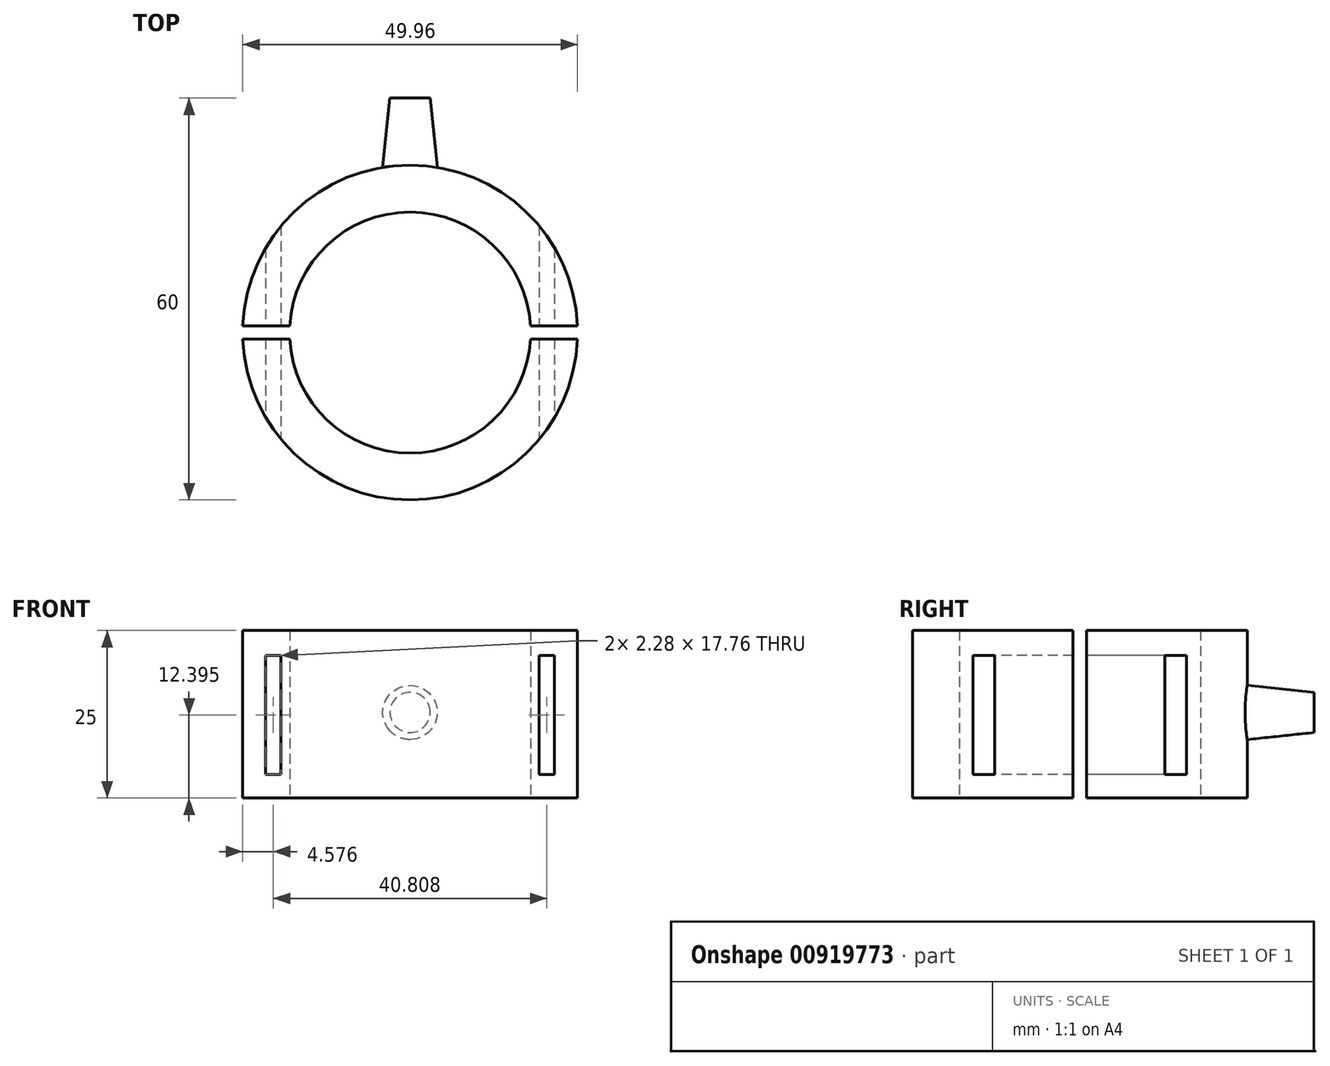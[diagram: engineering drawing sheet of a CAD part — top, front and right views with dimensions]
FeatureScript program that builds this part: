
annotation { "Feature Type Name" : "Feature", "Feature Type Description" : "" }
export const myFeature = defineFeature(function(context is Context, id is Id, definition is map)
    precondition{}
    {
        {
            var Q0;
            Q0=qCreatedBy(makeId("Top.planeOp"),FACE);
            var sketch = newSketch(context, id + "F0", { "sketchPlane" : qUnion([Q0])});
            skArc(sketch, "E0", {"start": v(-17.97, -1) * mm, "mid": v(0, -18) * mm, "end": v(17.97, -1) * mm});
            skArc(sketch, "E1.0", {"start": v(-24.98, -1) * mm, "mid": v(0, -25) * mm, "end": v(24.98, -1) * mm});
            skLineSegment(sketch, "E2.bottom", {"start": v(24.98, -1) * mm, "end": v(17.97, -1) * mm});
            skLineSegment(sketch, "E2.top", {"start": v(24.98, 1) * mm, "end": v(17.97, 1) * mm});
            skArc(sketch, "E3.trimOffspring", {"start": v(17.97, 1) * mm, "mid": v(0, 18) * mm, "end": v(-17.97, 1) * mm});
            skArc(sketch, "E4.trimOffspring", {"start": v(24.98, 1) * mm, "mid": v(0, 25) * mm, "end": v(-24.98, 1) * mm});
            skPoint(sketch, "E2.left.end.orphan", {"position": v(28.5, 1) * mm});
            skPoint(sketch, "E2.left.start.orphan", {"position": v(28.5, -1) * mm});
            skLineSegment(sketch, "E5.trimOffspring", {"start": v(-17.97, 1) * mm, "end": v(-24.98, 1) * mm});
            skLineSegment(sketch, "E6.trimOffspring", {"start": v(-17.97, -1) * mm, "end": v(-24.98, -1) * mm});
            skPoint(sketch, "E2.right.end.orphan", {"position": v(-28.5, 1) * mm});
            skPoint(sketch, "E7.orphan", {"position": v(-28.5, -1) * mm});
            skSolve(sketch);
        }
        {
            var Q0;
            Q0=makeQuery(id+"F0.imprint","IMPRINT",FACE,{"disambiguationData":[TD([[makeQuery(id+"F0.imprint","IMPRINT",EDGE,{"derivedFrom":sQuery(id+"F0.wireOp",EDGE,"E2.top")}),-1.0]])]});
            var Q1;
            Q1=makeQuery(id+"F0.imprint","IMPRINT",FACE,{"disambiguationData":[TD([[makeQuery(id+"F0.imprint","IMPRINT",EDGE,{"derivedFrom":sQuery(id+"F0.wireOp",EDGE,"E0")}),-1.0]])]});
            extrude(context, id + "F1", {"entities" : qUnion([Q0, Q1]), "depth" : 25 * mm, "offsetDistance" : 25 * mm});
        }
        {
            var Q0;
            Q0=qCreatedBy(makeId("Front.planeOp"),FACE);
            var sketch = newSketch(context, id + "F2", { "sketchPlane" : qUnion([Q0])});
            skLineSegment(sketch, "E8.bottom", {"start": v(21.54, 21.28) * mm, "end": v(19.26, 21.28) * mm});
            skLineSegment(sketch, "E8.top", {"start": v(21.54, 3.51) * mm, "end": v(19.26, 3.51) * mm});
            skLineSegment(sketch, "E8.left", {"start": v(21.54, 21.28) * mm, "end": v(21.54, 3.51) * mm});
            skLineSegment(sketch, "E8.right", {"start": v(19.26, 21.28) * mm, "end": v(19.26, 3.51) * mm});
            skPoint(sketch, "E8.middle", {"position": v(20.4, 12.4) * mm});
            skPoint(sketch, "E9.MirrorP", {"position": v(-20.4, 12.4) * mm});
            skLineSegment(sketch, "E10.MirrorCS", {"start": v(-21.54, 21.28) * mm, "end": v(-21.54, 3.51) * mm});
            skLineSegment(sketch, "E11.MirrorCS", {"start": v(-21.54, 21.28) * mm, "end": v(-19.26, 21.28) * mm});
            skLineSegment(sketch, "E12.MirrorCS", {"start": v(-19.26, 21.28) * mm, "end": v(-19.26, 3.51) * mm});
            skLineSegment(sketch, "E13.MirrorCS", {"start": v(-21.54, 3.51) * mm, "end": v(-19.26, 3.51) * mm});
            skSolve(sketch);
        }
        {
            var Q0;
            Q0 = qSketchRegion(id + "F2", true);
            extrude(context, id + "F3", {"entities" : qUnion([Q0]), "operationType" : NewBodyOperationType.REMOVE, "oppositeDirection" : true, "depth" : 25 * mm, "offsetDistance" : 25 * mm, "hasSecondDirection" : true, "secondDirectionOppositeDirection" : false, "secondDirectionDepth" : 25 * mm});
        }
        {
            var Q0;
            Q0=qCreatedBy(makeId("Front.planeOp"),FACE);
            cPlane(context, id + "F4", {"entities" : qUnion([Q0]), "cplaneType" : CPlaneType.OFFSET, "offset" : 35 * mm, "oppositeDirection" : true, "width" : 150 * mm, "height" : 150 * mm});
        }
        {
            var Q0;
            Q0=qCreatedBy(id+"F4.planeOp",FACE);
            var sketch = newSketch(context, id + "F5", { "sketchPlane" : qUnion([Q0])});
            skPoint(sketch, "E14.middle", {"position": v(0, 12.78) * mm});
            skCircle(sketch, "E15", {"center": v(0, 12.78) * mm, "radius": 3 * mm});
            skSolve(sketch);
        }
        {
            var Q0;
            Q0 = qSketchRegion(id + "F5", true);
            extrude(context, id + "F6", {"entities" : qUnion([Q0]), "operationType" : NewBodyOperationType.ADD, "depth" : 13.8 * mm, "offsetDistance" : 25 * mm, "hasDraft" : true, "draftAngle" : 6 * degree});
        }
    });
